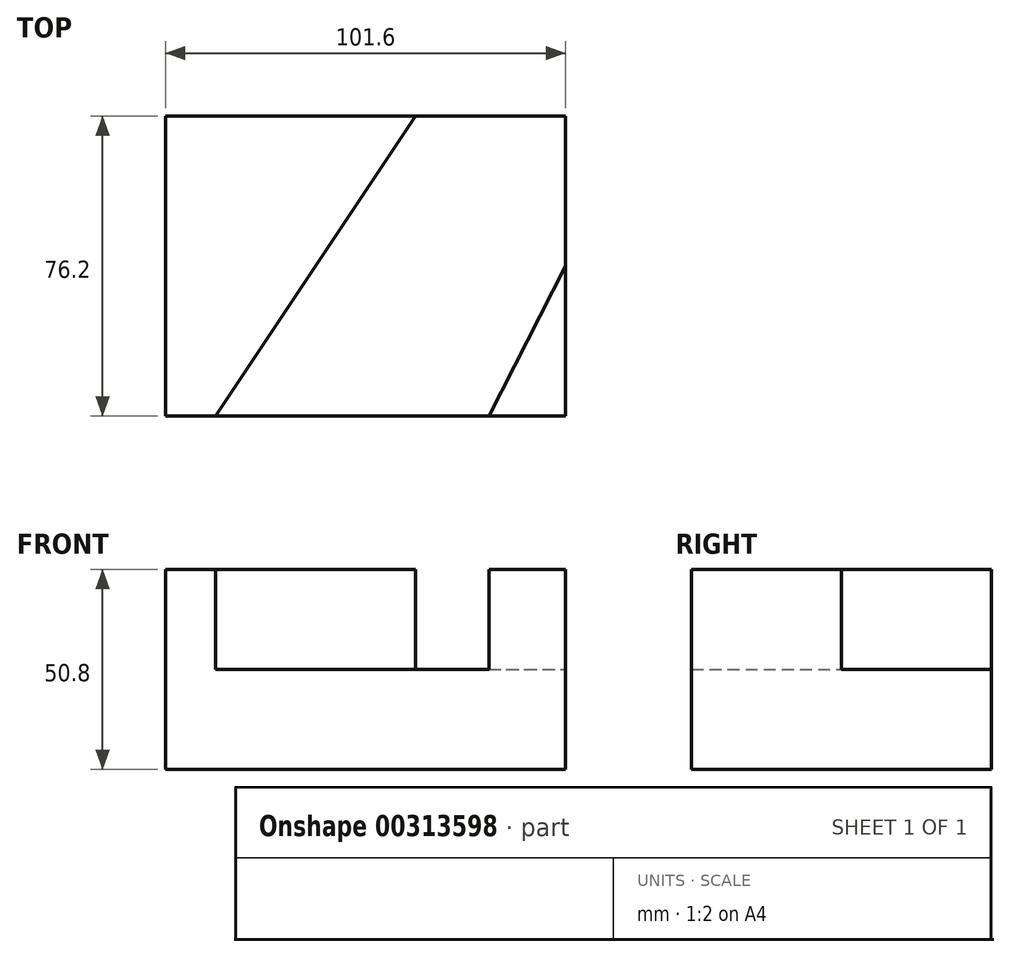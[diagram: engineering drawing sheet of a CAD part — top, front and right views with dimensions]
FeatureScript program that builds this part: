
annotation { "Feature Type Name" : "Feature", "Feature Type Description" : "" }
export const myFeature = defineFeature(function(context is Context, id is Id, definition is map)
    precondition{}
    {
        {
            var Q0;
            Q0=qCreatedBy(makeId("Top.planeOp"),FACE);
            var sketch = newSketch(context, id + "F0", { "sketchPlane" : qUnion([Q0])});
            skLineSegment(sketch, "E0.bottom", {"start": v(-46.83, 24.92) * mm, "end": v(54.77, 24.92) * mm});
            skLineSegment(sketch, "E0.top", {"start": v(-46.83, -51.28) * mm, "end": v(54.77, -51.28) * mm});
            skLineSegment(sketch, "E0.left", {"start": v(-46.83, 24.92) * mm, "end": v(-46.83, -51.28) * mm});
            skLineSegment(sketch, "E0.right", {"start": v(54.77, 24.92) * mm, "end": v(54.77, -51.28) * mm});
            skSolve(sketch);
        }
        {
            var Q0;
            Q0=makeQuery(id+"F0.imprint","IMPRINT",FACE,{"disambiguationData":[TD([[makeQuery(id+"F0.imprint","IMPRINT",EDGE,{"derivedFrom":sQuery(id+"F0.wireOp",EDGE,"E0.bottom")}),-1.0]])]});
            extrude(context, id + "F1", {"entities" : qUnion([Q0]), "oppositeDirection" : true, "depth" : 25.4 * mm});
        }
        {
            var Q0;
            Q0=makeQuery(id+"F1.opExtrude","CAP_FACE",FACE,{"disambiguationData":[OSD([sQuery(id+"F0.wireOp",EDGE,"E0.bottom"),sQuery(id+"F0.wireOp",EDGE,"E0.top"),sQuery(id+"F0.wireOp",EDGE,"E0.left"),sQuery(id+"F0.wireOp",EDGE,"E0.right")])],"isStart":true});
            var sketch = newSketch(context, id + "F2", { "sketchPlane" : qUnion([Q0])});
            skLineSegment(sketch, "E1", {"start": v(35.32, -51.28) * mm, "end": v(54.77, -13.18) * mm});
            skLineSegment(sketch, "E2", {"start": v(-34.13, -51.28) * mm, "end": v(16.67, 24.92) * mm});
            skLineSegment(sketch, "E3", {"start": v(16.67, 24.92) * mm, "end": v(-46.83, 24.92) * mm});
            skLineSegment(sketch, "E4", {"start": v(-34.13, -51.28) * mm, "end": v(-46.83, -51.28) * mm});
            skSolve(sketch);
        }
        {
            var Q0;
            Q0=makeQuery(id+"F2.imprint","IMPRINT",FACE,{"disambiguationData":[TD([[makeQuery(id+"F2.imprint","IMPRINT",EDGE,{"derivedFrom":sQuery(id+"F2.wireOp",EDGE,"E2")}),1.0]])]});
            extrude(context, id + "F3", {"entities" : qUnion([Q0]), "operationType" : NewBodyOperationType.ADD, "depth" : 25.4 * mm});
        }
        {
            var Q0;
            {var subQ0=sQuery(id+"F2.wireOp",EDGE,"E1");Q0=makeQuery(id+"F2.imprint","IMPRINT",FACE,{"disambiguationData":[TD([[makeQuery(id+"F2.imprint","IMPRINT",EDGE,{"derivedFrom":subQ0}),-1.0]])]});}
            extrude(context, id + "F4", {"entities" : qUnion([Q0]), "operationType" : NewBodyOperationType.ADD, "depth" : 25.4 * mm});
        }
    });
